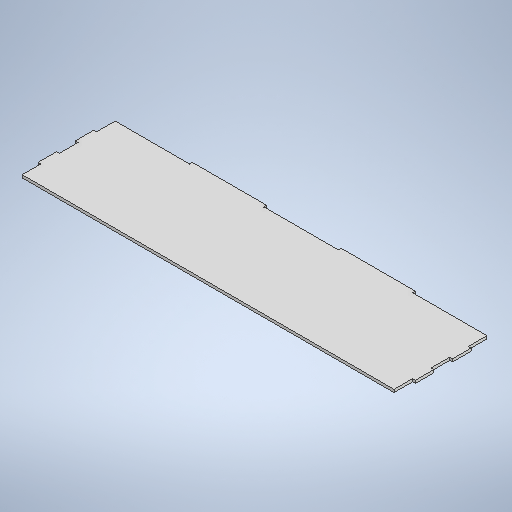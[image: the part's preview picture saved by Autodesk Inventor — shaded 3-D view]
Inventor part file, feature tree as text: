
AUTODESK INVENTOR PART (.ipt)
format: ipt  version: 2025.1 (Build 291241020, 241B)  size: 261,120 bytes
history: native  units: mm
features: extrude x1, sketch x1
ambient origin geometry x8: Origin, YZ Plane, XZ Plane, XY Plane, X Axis, Y Axis, Z Axis, Center Point
bodies: Solid1 (feature_tree)
feature tree (2):
  extrude  "Extrusion1"  Depth=3.0mm
  sketch  "Sketch1"  dims[d1=100.0mm d7=3.0mm d8=80.0mm d14=3.0mm d15=0.0mm d17=20.0mm d18=20.0mm d19=20.0mm]
